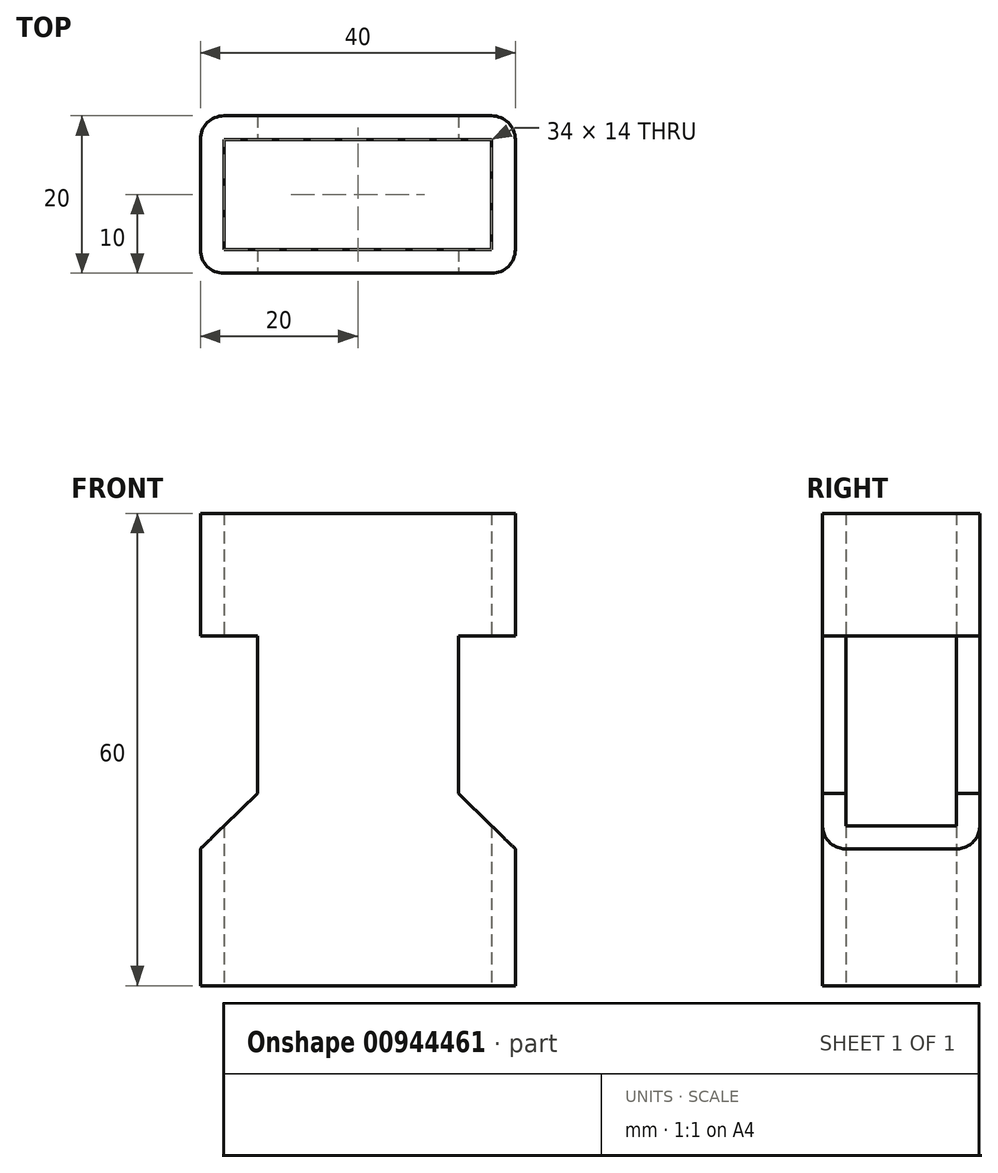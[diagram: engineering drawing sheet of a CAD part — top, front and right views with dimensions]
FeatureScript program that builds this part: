
annotation { "Feature Type Name" : "Feature", "Feature Type Description" : "" }
export const myFeature = defineFeature(function(context is Context, id is Id, definition is map)
    precondition{}
    {
        {
            var Q0;
            Q0=qCreatedBy(makeId("Top.planeOp"),FACE);
            var sketch = newSketch(context, id + "F0", { "sketchPlane" : qUnion([Q0])});
            skLineSegment(sketch, "E0.bottom", {"start": v(17, -10) * mm, "end": v(-17, -10) * mm});
            skLineSegment(sketch, "E0.top", {"start": v(17, 10) * mm, "end": v(-17, 10) * mm});
            skLineSegment(sketch, "E0.left", {"start": v(20, -7) * mm, "end": v(20, 7) * mm});
            skLineSegment(sketch, "E0.right", {"start": v(-20, -7) * mm, "end": v(-20, 7) * mm});
            skPoint(sketch, "E0.middle", {"position": v(0, 0) * mm});
            skPoint(sketch, "E1.visualSharp", {"position": v(-20, 10) * mm});
            skArc(sketch, "E1.filletArc", {"start": v(-17, 10) * mm, "mid": v(-19.12, 9.12) * mm, "end": v(-20, 7) * mm});
            skPoint(sketch, "E2.visualSharp", {"position": v(20, 10) * mm});
            skArc(sketch, "E2.filletArc", {"start": v(20, 7) * mm, "mid": v(19.12, 9.12) * mm, "end": v(17, 10) * mm});
            skPoint(sketch, "E3.visualSharp", {"position": v(20, -10) * mm});
            skArc(sketch, "E3.filletArc", {"start": v(17, -10) * mm, "mid": v(19.12, -9.12) * mm, "end": v(20, -7) * mm});
            skPoint(sketch, "E4.visualSharp", {"position": v(-20, -10) * mm});
            skArc(sketch, "E4.filletArc", {"start": v(-20, -7) * mm, "mid": v(-19.12, -9.12) * mm, "end": v(-17, -10) * mm});
            skLineSegment(sketch, "E5.0", {"start": v(17, 7) * mm, "end": v(-17, 7) * mm});
            skLineSegment(sketch, "E6.0", {"start": v(-17, -7) * mm, "end": v(-17, 7) * mm});
            skLineSegment(sketch, "E7.0", {"start": v(17, -7) * mm, "end": v(-17, -7) * mm});
            skLineSegment(sketch, "E8.0", {"start": v(17, -7) * mm, "end": v(17, 7) * mm});
            skSolve(sketch);
        }
        {
            var Q0;
            Q0=makeQuery(id+"F0.imprint","IMPRINT",FACE,{"disambiguationData":[TD([[makeQuery(id+"F0.imprint","IMPRINT",EDGE,{"derivedFrom":sQuery(id+"F0.wireOp",EDGE,"E0.bottom")}),-1.0]])]});
            extrude(context, id + "F1", {"entities" : qUnion([Q0]), "depth" : 60 * mm, "offsetDistance" : 25 * mm});
        }
        {
            var Q0;
            Q0=qCreatedBy(makeId("Front.planeOp"),FACE);
            var sketch = newSketch(context, id + "F2", { "sketchPlane" : qUnion([Q0])});
            skLineSegment(sketch, "E9", {"start": v(-22.85, 14.58) * mm, "end": v(-12.76, 24.45) * mm});
            skLineSegment(sketch, "E10", {"start": v(-12.76, 24.45) * mm, "end": v(-12.76, 44.4) * mm});
            skLineSegment(sketch, "E11", {"start": v(-12.76, 44.4) * mm, "end": v(-25.04, 44.4) * mm});
            skLineSegment(sketch, "E12", {"start": v(-25.04, 44.4) * mm, "end": v(-22.85, 14.58) * mm});
            skLineSegment(sketch, "E13.MirrorCS", {"start": v(25.04, 44.4) * mm, "end": v(22.85, 14.58) * mm});
            skLineSegment(sketch, "E14.MirrorCS", {"start": v(12.76, 44.4) * mm, "end": v(25.04, 44.4) * mm});
            skLineSegment(sketch, "E15.MirrorCS", {"start": v(12.76, 24.45) * mm, "end": v(12.76, 44.4) * mm});
            skLineSegment(sketch, "E16.MirrorCS", {"start": v(22.85, 14.58) * mm, "end": v(12.76, 24.45) * mm});
            skSolve(sketch);
        }
        {
            var Q0;
            Q0=makeQuery(id+"F2.imprint","IMPRINT",FACE,{"disambiguationData":[TD([[makeQuery(id+"F2.imprint","IMPRINT",EDGE,{"derivedFrom":sQuery(id+"F2.wireOp",EDGE,"E9")}),1.0]])]});
            var Q1;
            Q1=makeQuery(id+"F2.imprint","IMPRINT",FACE,{"disambiguationData":[TD([[makeQuery(id+"F2.imprint","IMPRINT",EDGE,{"derivedFrom":sQuery(id+"F2.wireOp",EDGE,"E13.MirrorCS")}),-1.0]])]});
            extrude(context, id + "F3", {"entities" : qUnion([Q0, Q1]), "operationType" : NewBodyOperationType.REMOVE, "endBound" : BoundingType.SYMMETRIC, "oppositeDirection" : true, "depth" : 25 * mm, "offsetDistance" : 25 * mm});
        }
    });
